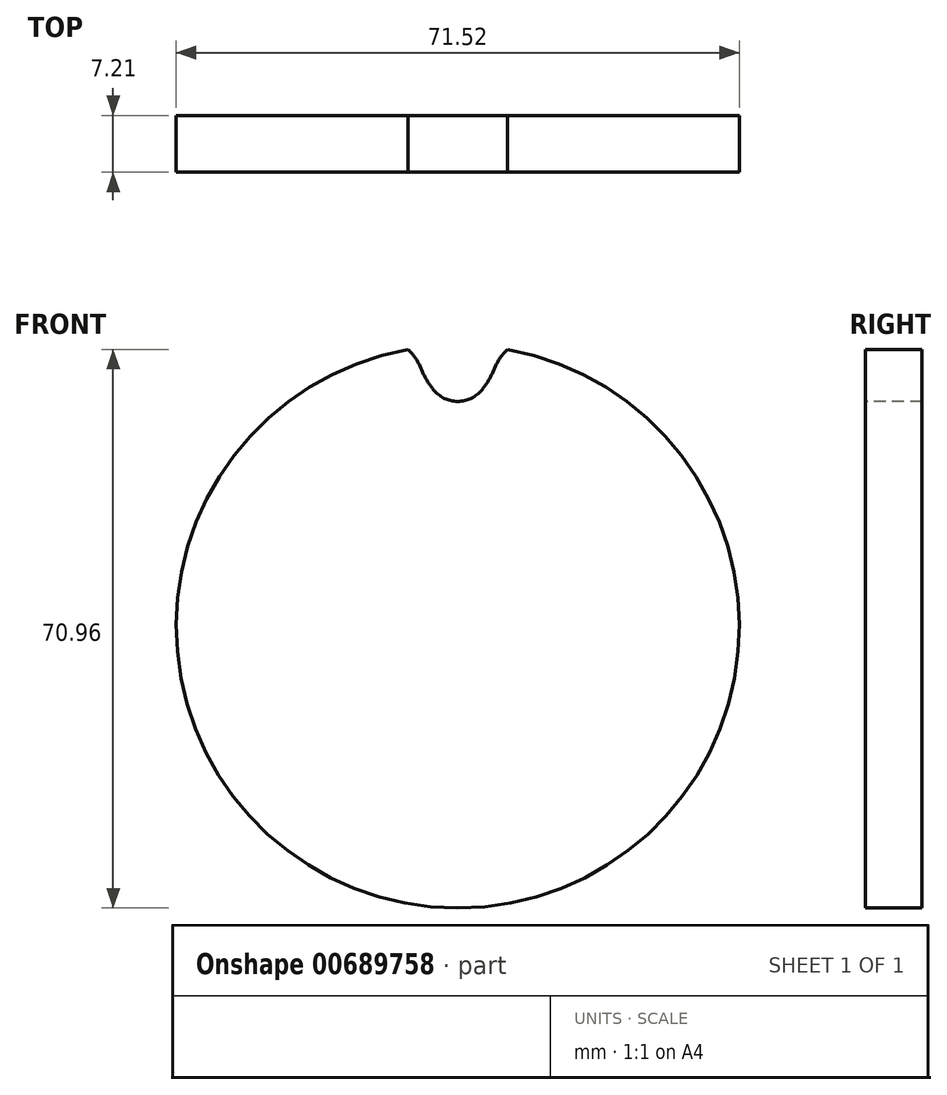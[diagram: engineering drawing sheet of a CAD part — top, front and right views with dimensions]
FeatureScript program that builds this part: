
annotation { "Feature Type Name" : "Feature", "Feature Type Description" : "" }
export const myFeature = defineFeature(function(context is Context, id is Id, definition is map)
    precondition{}
    {
        {
            var Q0;
            Q0=qCreatedBy(makeId("Front.planeOp"),FACE);
            var sketch = newSketch(context, id + "F0", { "sketchPlane" : qUnion([Q0])});
            skCircle(sketch, "E0", {"center": v(0, 0) * mm, "radius": 35.76 * mm});
            skSolve(sketch);
        }
        {
            var Q0;
            Q0=qSketchRegion(id+"F0",true);
            extrude(context, id + "F1", {"entities" : qUnion([Q0]), "oppositeDirection" : true, "depth" : 7.2 * mm});
        }
        {
            var Q0;
            Q0=makeQuery(id+"F1.opExtrude","CAP_FACE",FACE,{"disambiguationData":[OSD([sQuery(id+"F0.wireOp",EDGE,"E0")])],"isStart":true});
            var sketch = newSketch(context, id + "F2", { "sketchPlane" : qUnion([Q0])});
            skCircle(sketch, "E1", {"center": v(0, 0) * mm, "radius": 32.55 * mm, "construction": true});
            skLineSegment(sketch, "E2", {"start": v(0, 0) * mm, "end": v(0, 32.55) * mm, "construction": true});
            skLineSegment(sketch, "E3", {"start": v(0, 32.55) * mm, "end": v(75.89, 32.55) * mm, "construction": true});
            skLineSegment(sketch, "E4", {"start": v(0, 32.55) * mm, "end": v(5, 36.56) * mm, "construction": true});
            skLineSegment(sketch, "E5", {"start": v(5, 36.56) * mm, "end": v(-4.46, 32.3) * mm, "construction": true});
            skLineSegment(sketch, "E6", {"start": v(-4.46, 32.3) * mm, "end": v(-4.82, 33.1) * mm});
            skLineSegment(sketch, "E7", {"start": v(0, 0) * mm, "end": v(-7.13, 35.85) * mm, "construction": true});
            skArc(sketch, "E8", {"start": v(-7.13, 35.85) * mm, "mid": v(-15.87, 26.15) * mm, "end": v(-4.82, 33.1) * mm, "construction": true});
            skArc(sketch, "E9", {"start": v(-4.82, 33.1) * mm, "mid": v(-5.78, 34.63) * mm, "end": v(-7.13, 35.85) * mm});
            skLineSegment(sketch, "E10", {"start": v(0.64, 20.98) * mm, "end": v(-4.82, 33.1) * mm, "construction": true});
            skArc(sketch, "E11", {"start": v(-4.46, 32.3) * mm, "mid": v(-3.84, 31.14) * mm, "end": v(-3.1, 30.07) * mm});
            skArc(sketch, "E12", {"start": v(-3.1, 30.07) * mm, "mid": v(13.83, 41.97) * mm, "end": v(-4.46, 32.3) * mm, "construction": true});
            skArc(sketch, "E13.0.MirrorCS", {"start": v(4.46, 32.3) * mm, "mid": v(3.84, 31.14) * mm, "end": v(3.1, 30.07) * mm});
            skLineSegment(sketch, "E14.0.MirrorCS", {"start": v(4.46, 32.3) * mm, "end": v(4.82, 33.1) * mm});
            skArc(sketch, "E15.0.MirrorCS", {"start": v(4.82, 33.1) * mm, "mid": v(5.78, 34.63) * mm, "end": v(7.13, 35.85) * mm});
            skArc(sketch, "E16", {"start": v(-3.1, 30.07) * mm, "mid": v(0, 28.59) * mm, "end": v(3.1, 30.07) * mm});
            skArc(sketch, "E17", {"start": v(3.1, 30.07) * mm, "mid": v(0, 36.51) * mm, "end": v(-3.1, 30.07) * mm, "construction": true});
            skLineSegment(sketch, "E18.anchor1", {"start": v(0, 0) * mm, "end": v(4.82, 33.1) * mm, "construction": true});
            skLineSegment(sketch, "E18.anchor2", {"start": v(0, 0) * mm, "end": v(4.82, 33.1) * mm, "construction": true});
            skArc(sketch, "E19", {"start": v(7.13, 35.85) * mm, "mid": v(0, 37.75) * mm, "end": v(-7.13, 35.85) * mm});
            skSolve(sketch);
        }
        {
            var Q0;
            {var subQ4=sQuery(id+"F2.wireOp",EDGE,"E6");Q0=makeQuery(id+"F2.imprint","IMPRINT",FACE,{"disambiguationData":[TD([[makeQuery(id+"F2.imprint","IMPRINT",EDGE,{"derivedFrom":subQ4}),-1.0]])]});}
            extrude(context, id + "F3", {"entities" : qUnion([Q0]), "operationType" : NewBodyOperationType.REMOVE, "endBound" : BoundingType.THROUGH_ALL, "oppositeDirection" : true, "depth" : 25.4 * mm});
        }
    });
